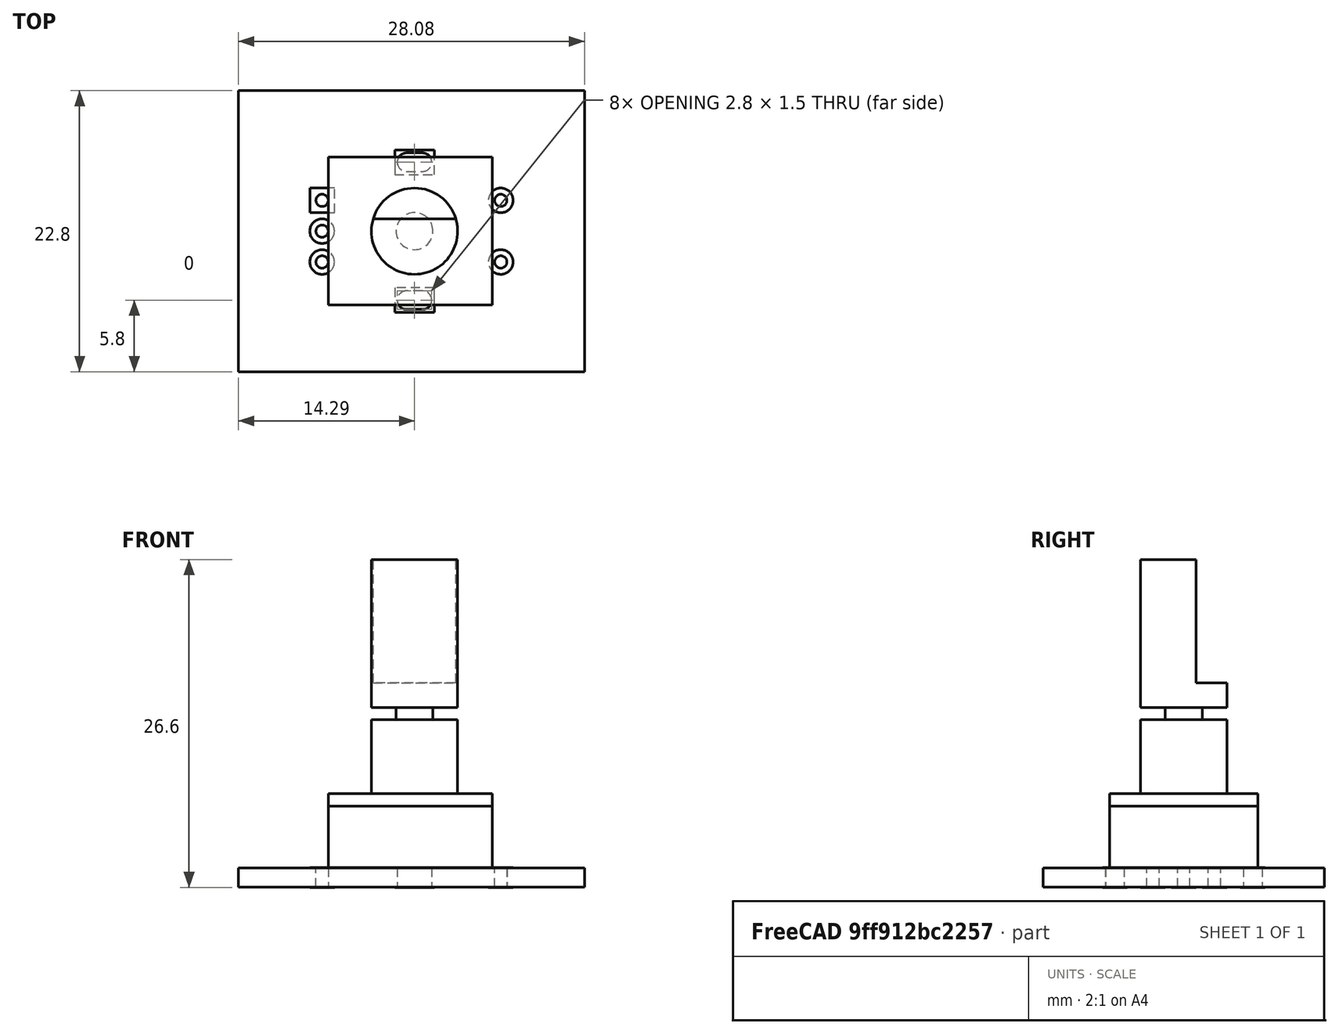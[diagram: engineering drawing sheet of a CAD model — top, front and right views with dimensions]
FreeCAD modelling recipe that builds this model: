
FCSTD DOCUMENT  (FreeCAD 0.18R16146 (Git))
Label: rotary
License: All rights reserved
LicenseURL: http://en.wikipedia.org/wiki/All_rights_reserved
objects: Part::FeaturePython×7, Part::Cylinder×3, Part::Feature×3, App::DocumentObjectGroup×1, Part::Box×1, Part::Cut×1
note: 15 computed .brp shape members not serialized (recipe doc carries the construction recipe); baked Part::Feature solids carry a one-line shape summary decoded from their .brp

FEATURE [Part::FeaturePython] FCrtYd_lines  label="FCrtYd"  # a2plus imported part (geometry in sourceFile) (typed FeaturePython)
  fixedPosition = true
FEATURE [Part::FeaturePython] FFab_lines  label="FFab"  # a2plus imported part (geometry in sourceFile) (typed FeaturePython)
  fixedPosition = true
FEATURE [Part::FeaturePython] Filk_lines  label="FrontSilk"  # a2plus imported part (geometry in sourceFile) (typed FeaturePython)
  fixedPosition = true
FEATURE [Part::FeaturePython] TopPads  # a2plus imported part (geometry in sourceFile) (typed FeaturePython)
  fixedPosition = true
FEATURE [Part::FeaturePython] BotPads  # a2plus imported part (geometry in sourceFile) (typed FeaturePython)
  fixedPosition = true
FEATURE [Part::FeaturePython] THPs  label="PTHs"  # a2plus imported part (geometry in sourceFile) (typed FeaturePython)
  fixedPosition = true
FEATURE [Part::FeaturePython] newPCB  label="Pcb"  # a2plus imported part (geometry in sourceFile) (typed FeaturePython)
  fixedPosition = true
FEATURE [App::DocumentObjectGroup] RotaryEncoder_Alps_EC11E_Switch_Vertical_H20mm_fp
  Group = -> [FCrtYd_lines,FFab_lines,Filk_lines,TopPads,BotPads,THPs,newPCB]
FEATURE [Part::Cylinder] Cylinder  label="Zylinder"
  Angle = 360
  AttacherType = Attacher::AttachEngine3D
  Height = 6
  Placement = pos=(7.5,-2.5,6) rot=(0,0,1;0rad)
  Radius = 3.5
FEATURE [Part::Cylinder] Cylinder001  label="Zylinder001"
  Angle = 360
  AttacherType = Attacher::AttachEngine3D
  Height = 1
  Placement = pos=(7.5,-2.5,12) rot=(0,0,1;0rad)
  Radius = 1.5
FEATURE [Part::Cylinder] Cylinder002  label="Zylinder002"
  Angle = 360
  AttacherType = Attacher::AttachEngine3D
  Height = 12
  Placement = pos=(7.5,-2.5,13) rot=(0,0,1;0rad)
  Radius = 3.5
FEATURE [Part::Box] Box001  label="Würfel001"
  AttacherType = Attacher::AttachEngine3D
  Height = 10
  Length = 10
  Placement = pos=(2,-1.5,15) rot=(0,0,1;0rad)
  Width = 10
FEATURE [Part::Cut] Cut
  Base = -> Cylinder002
  Tool = -> Box001
FEATURE [Part::Feature] Shape001  label="top"
  shape: bbox 13.3 x 12 x 1 mm, 6 faces (baked)
FEATURE [Part::Feature] Shape002  label="bottom"
  shape: bbox 13.3 x 12 x 5 mm, 6 faces (baked)
FEATURE [Part::Feature] Shape  label="shaft"
  shape: bbox 7 x 7 x 19 mm, 9 faces (baked)
